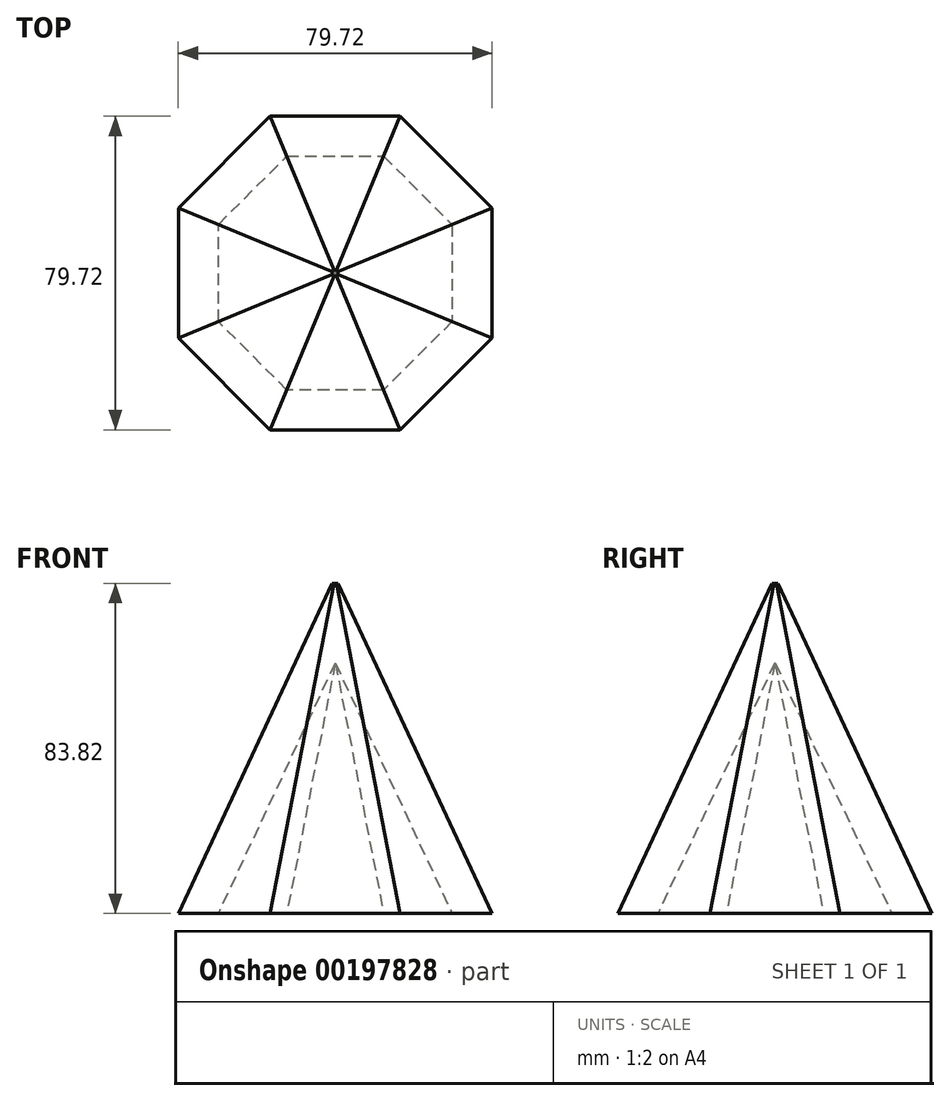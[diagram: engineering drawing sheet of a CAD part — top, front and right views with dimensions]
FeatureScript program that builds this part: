
annotation { "Feature Type Name" : "Feature", "Feature Type Description" : "" }
export const myFeature = defineFeature(function(context is Context, id is Id, definition is map)
    precondition{}
    {
        {
            var Q0;
            Q0=qCreatedBy(makeId("Top.planeOp"),FACE);
            var sketch = newSketch(context, id + "F0", { "sketchPlane" : qUnion([Q0])});
            skCircle(sketch, "E0.cCircle", {"center": v(0, 0) * mm, "radius": 39.86 * mm, "construction": true});
            skLineSegment(sketch, "E0.0", {"start": v(-16.51, 39.86) * mm, "end": v(16.51, 39.86) * mm});
            skLineSegment(sketch, "E0.1", {"start": v(16.51, 39.86) * mm, "end": v(39.86, 16.51) * mm});
            skLineSegment(sketch, "E0.2", {"start": v(39.86, 16.51) * mm, "end": v(39.86, -16.51) * mm});
            skLineSegment(sketch, "E0.3", {"start": v(39.86, -16.51) * mm, "end": v(16.51, -39.86) * mm});
            skLineSegment(sketch, "E0.4", {"start": v(16.51, -39.86) * mm, "end": v(-16.51, -39.86) * mm});
            skLineSegment(sketch, "E0.5", {"start": v(-16.51, -39.86) * mm, "end": v(-39.86, -16.51) * mm});
            skLineSegment(sketch, "E0.6", {"start": v(-39.86, -16.51) * mm, "end": v(-39.86, 16.5) * mm});
            skLineSegment(sketch, "E0.7", {"start": v(-39.86, 16.5) * mm, "end": v(-16.51, 39.86) * mm});
            skPoint(sketch, "E0.0.midPoint", {"position": v(0, 39.86) * mm});
            skCircle(sketch, "E1.cCircle", {"center": v(0, 0) * mm, "radius": 29.7 * mm, "construction": true});
            skLineSegment(sketch, "E1.0", {"start": v(-12.3, 29.7) * mm, "end": v(12.3, 29.7) * mm});
            skLineSegment(sketch, "E1.1", {"start": v(12.3, 29.7) * mm, "end": v(29.7, 12.3) * mm});
            skLineSegment(sketch, "E1.2", {"start": v(29.7, 12.3) * mm, "end": v(29.7, -12.3) * mm});
            skLineSegment(sketch, "E1.3", {"start": v(29.7, -12.3) * mm, "end": v(12.3, -29.7) * mm});
            skLineSegment(sketch, "E1.4", {"start": v(12.3, -29.7) * mm, "end": v(-12.3, -29.7) * mm});
            skLineSegment(sketch, "E1.5", {"start": v(-12.3, -29.7) * mm, "end": v(-29.7, -12.3) * mm});
            skLineSegment(sketch, "E1.6", {"start": v(-29.7, -12.3) * mm, "end": v(-29.7, 12.3) * mm});
            skLineSegment(sketch, "E1.7", {"start": v(-29.7, 12.3) * mm, "end": v(-12.3, 29.7) * mm});
            skPoint(sketch, "E1.0.midPoint", {"position": v(0, 29.7) * mm});
            skSolve(sketch);
        }
        {
            var Q0;
            Q0 = qSketchRegion(id + "F0", true);
            var Q1;
            Q1=makeQuery(id+"F0.imprint","IMPRINT",FACE,{"disambiguationData":[TD([[makeQuery(id+"F0.imprint","IMPRINT",EDGE,{"derivedFrom":sQuery(id+"F0.wireOp",EDGE,"E1.0")}),-1.0]])]});
            extrude(context, id + "F1", {"entities" : qUnion([Q0, Q1]), "depth" : 83.82 * mm, "hasDraft" : true, "draftAngle" : 25 * degree, "draftPullDirection" : true});
        }
        {
            var Q0;
            Q0=qCreatedBy(makeId("Top.planeOp"),FACE);
            var sketch = newSketch(context, id + "F2", { "sketchPlane" : qUnion([Q0])});
            skCircle(sketch, "E2.cCircle", {"center": v(0, 0) * mm, "radius": 29.7 * mm, "construction": true});
            skLineSegment(sketch, "E2.0", {"start": v(29.7, 12.3) * mm, "end": v(29.7, -12.3) * mm});
            skLineSegment(sketch, "E2.1", {"start": v(29.7, -12.3) * mm, "end": v(12.3, -29.7) * mm});
            skLineSegment(sketch, "E2.2", {"start": v(12.3, -29.7) * mm, "end": v(-12.3, -29.7) * mm});
            skLineSegment(sketch, "E2.3", {"start": v(-12.3, -29.7) * mm, "end": v(-29.7, -12.3) * mm});
            skLineSegment(sketch, "E2.4", {"start": v(-29.7, -12.3) * mm, "end": v(-29.7, 12.3) * mm});
            skLineSegment(sketch, "E2.5", {"start": v(-29.7, 12.3) * mm, "end": v(-12.3, 29.7) * mm});
            skLineSegment(sketch, "E2.6", {"start": v(-12.3, 29.7) * mm, "end": v(12.3, 29.7) * mm});
            skLineSegment(sketch, "E2.7", {"start": v(12.3, 29.7) * mm, "end": v(29.7, 12.3) * mm});
            skPoint(sketch, "E2.0.midPoint", {"position": v(29.7, 0) * mm});
            skSolve(sketch);
        }
        {
            var Q0;
            Q0 = qSketchRegion(id + "F2", true);
            extrude(context, id + "F3", {"entities" : qUnion([Q0]), "operationType" : NewBodyOperationType.REMOVE, "depth" : 63.5 * mm, "hasDraft" : true, "draftAngle" : 25 * degree, "draftPullDirection" : true});
        }
    });
